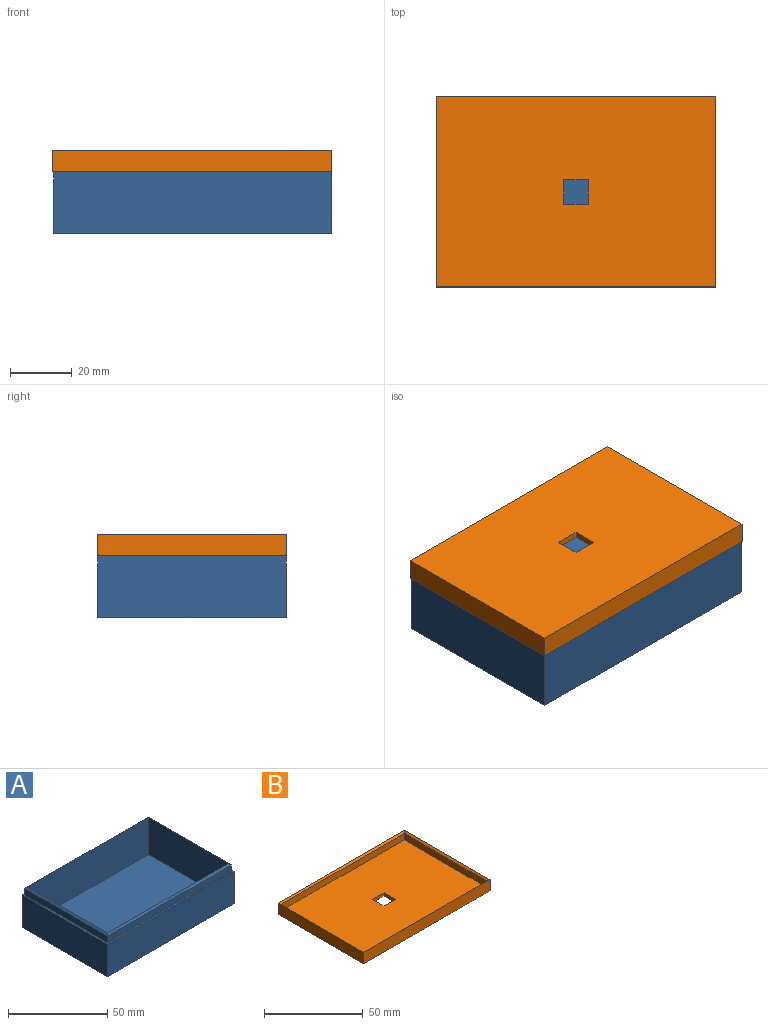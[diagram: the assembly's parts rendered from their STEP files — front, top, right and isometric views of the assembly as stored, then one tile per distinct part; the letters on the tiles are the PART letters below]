
ASSEMBLY  parts=2 mates=1
PART A: 19 faces, bbox 90x61x25 mm
  f0: plane 57x23mm, normal (1,0,0), area 1311mm2, adj f1,f3,f4,f15
  f1: plane 86x23mm, normal (0,1,0), area 1978mm2, adj f0,f2,f4,f16
  f2: plane 57x23mm, normal (-1,0,0), area 1311mm2, adj f1,f3,f4,f18
  f3: plane 86x23mm, normal (0,-1,0), area 1978mm2, adj f0,f2,f4,f17
  f4: plane 86x57mm, normal (0,0,1), area 4902mm2, adj f0,f1,f2,f3
  f5: plane 88x4mm, normal (0,-1,0), area 352mm2, adj f6,f8,f9,f16
  f6: plane 59x4mm, normal (-1,0,0), area 236mm2, adj f5,f7,f9,f15
  f7: plane 88x4mm, normal (0,1,0), area 352mm2, adj f6,f8,f9,f17
  f8: plane 59x4mm, normal (1,0,0), area 236mm2, adj f5,f7,f9,f18
  f9: plane 90x61mm, normal (0,0,1), area 298mm2, adj f5,f6,f7,f8,f11,f12,f13,f14
  f10: plane 90x61mm, normal (0,0,-1), area 5490mm2, adj f11,f12,f13,f14
  f11: plane 90x20mm, normal (0,1,0), area 1800mm2, adj f9,f10,f12,f14
  f12: plane 61x20mm, normal (1,0,0), area 1220mm2, adj f9,f10,f11,f13
  f13: plane 90x20mm, normal (0,-1,0), area 1800mm2, adj f9,f10,f12,f14
  f14: plane 61x20mm, normal (-1,0,0), area 1220mm2, adj f9,f10,f11,f13
  f15: plane 59x1mm, normal (-0.71,0,0.71), area 82mm2, adj f0,f6,f16,f17
  f16: plane 88x1mm, normal (0,-0.71,0.71), area 123mm2, adj f1,f5,f15,f18
  f17: plane 88x1mm, normal (0,0.71,0.71), area 123mm2, adj f3,f7,f15,f18
  f18: plane 59x1mm, normal (0.71,0,0.71), area 82mm2, adj f2,f8,f16,f17
PART B: 18 faces, bbox 90.5x61.5x7 mm
  f0: plane 88.5x59.5mm, normal (0,0,1), area 5201.8mm2, adj f6,f7,f8,f9,f14,f15,f16,f17
  f1: plane 90.5x7mm, normal (0,-1,0), area 633.5mm2, adj f2,f4,f5,f11
  f2: plane 61.5x7mm, normal (1,0,0), area 430.5mm2, adj f1,f3,f5,f13
  f3: plane 90.5x7mm, normal (0,1,0), area 633.5mm2, adj f2,f4,f5,f12
  f4: plane 61.5x7mm, normal (-1,0,0), area 430.5mm2, adj f1,f3,f5,f10
  f5: plane 90.5x61.5mm, normal (0,0,-1), area 5501.7mm2, adj f1,f2,f3,f4,f14,f15,f16,f17
  f6: plane 88.5x4mm, normal (0,1,0), area 354mm2, adj f0,f7,f8,f11
  f7: plane 59.5x4mm, normal (1,0,0), area 238mm2, adj f0,f6,f9,f10
  f8: plane 59.5x4mm, normal (-1,0,0), area 238mm2, adj f0,f6,f9,f13
  f9: plane 88.5x4mm, normal (0,-1,0), area 354mm2, adj f0,f7,f8,f12
  f10: plane 61.5x1mm, normal (0.71,0,0.71), area 85.6mm2, adj f4,f7,f11,f12
  f11: plane 90.5x1mm, normal (0,0.71,0.71), area 126.6mm2, adj f1,f6,f10,f13
  f12: plane 90.5x1mm, normal (0,-0.71,0.71), area 126.6mm2, adj f3,f9,f10,f13
  f13: plane 61.5x1mm, normal (-0.71,0,0.71), area 85.6mm2, adj f2,f8,f11,f12
  f14: plane 8x2mm, normal (0,1,0), area 16mm2, adj f0,f5,f15,f16
  f15: plane 8x2mm, normal (1,0,0), area 16mm2, adj f0,f5,f14,f17
  f16: plane 8x2mm, normal (-1,0,0), area 16mm2, adj f0,f5,f14,f17
  f17: plane 8x2mm, normal (0,-1,0), area 16mm2, adj f0,f5,f15,f16
PLACE A t=(-0.25,0,0)mm
PLACE B rot(axis=(1,0,0),180deg) t=(-0.5,0,27)mm
MATE fastened B.f2 <-> A.f12  axis (1,0,0) through (44.75,0,20)mm
